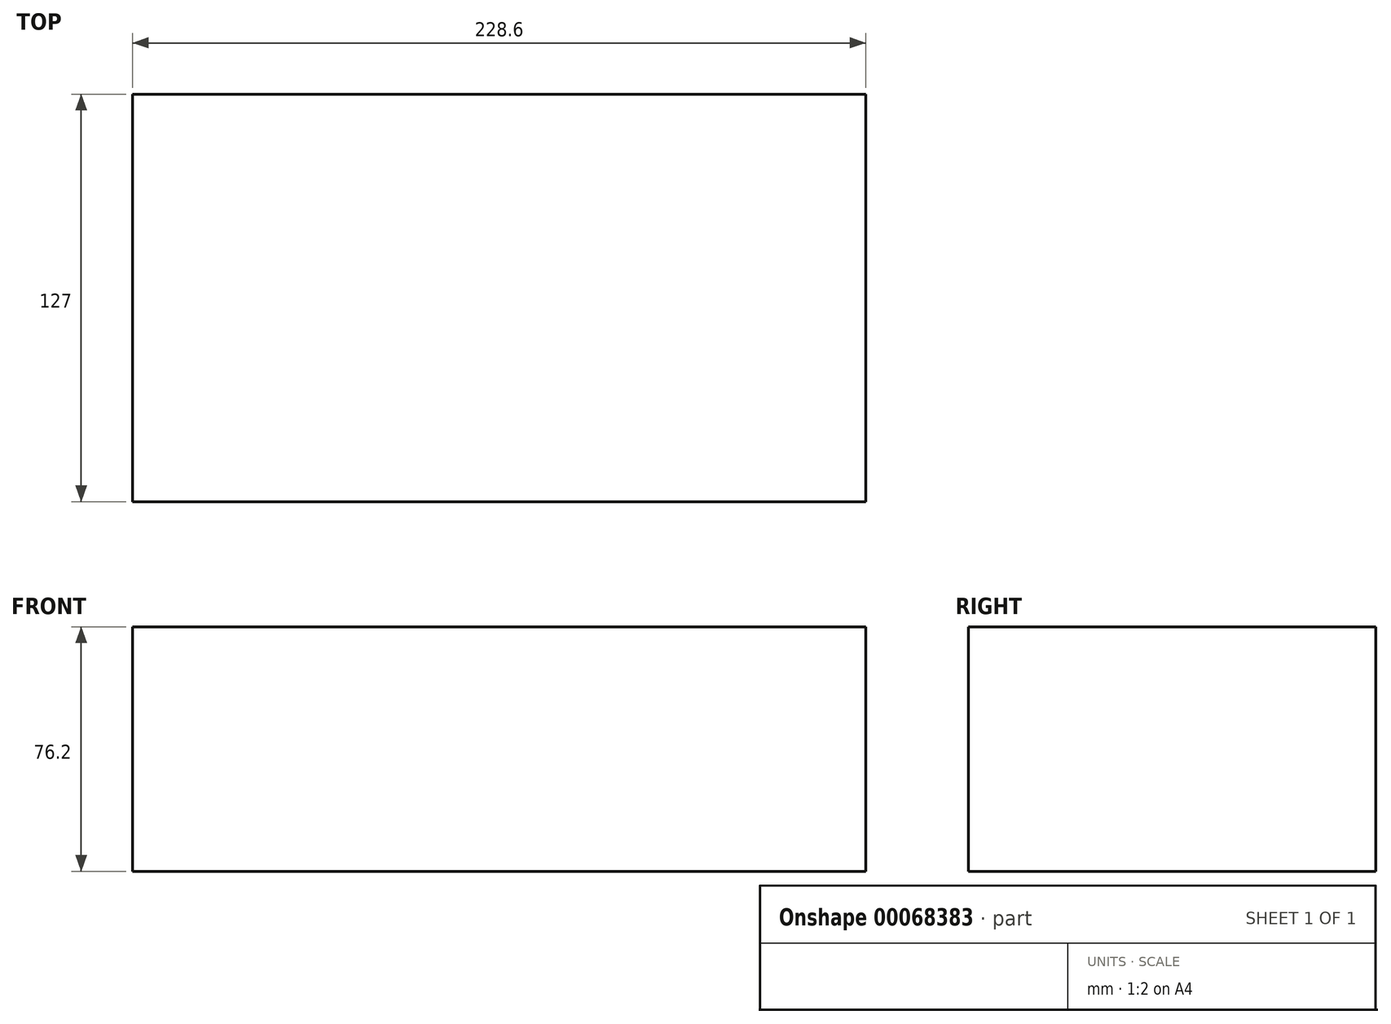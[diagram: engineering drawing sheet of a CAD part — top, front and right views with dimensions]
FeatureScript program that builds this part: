
annotation { "Feature Type Name" : "Feature", "Feature Type Description" : "" }
export const myFeature = defineFeature(function(context is Context, id is Id, definition is map)
    precondition{}
    {
        {
            var Q0;
            Q0=qCreatedBy(makeId("Top.planeOp"),FACE);
            var sketch = newSketch(context, id + "F0", { "sketchPlane" : qUnion([Q0])});
            skLineSegment(sketch, "E0.rect.bottom", {"start": v(-114.3, 63.5) * mm, "end": v(114.3, 63.5) * mm});
            skLineSegment(sketch, "E0.rect.top", {"start": v(-114.3, -63.5) * mm, "end": v(114.3, -63.5) * mm});
            skLineSegment(sketch, "E0.rect.left", {"start": v(-114.3, 63.5) * mm, "end": v(-114.3, -63.5) * mm});
            skLineSegment(sketch, "E0.rect.right", {"start": v(114.3, 63.5) * mm, "end": v(114.3, -63.5) * mm});
            skPoint(sketch, "E0.rect.middle", {"position": v(0, 0) * mm});
            skSolve(sketch);
        }
        {
            var Q0;
            Q0=makeQuery(id+"F0.imprint","IMPRINT",FACE,{"disambiguationData":[TD([[makeQuery(id+"F0.imprint","IMPRINT",EDGE,{"derivedFrom":sQuery(id+"F0.wireOp",EDGE,"E0.rect.bottom")}),-1.0]])]});
            extrude(context, id + "F1", {"entities" : qUnion([Q0]), "depth" : 76.2 * mm});
        }
    });
